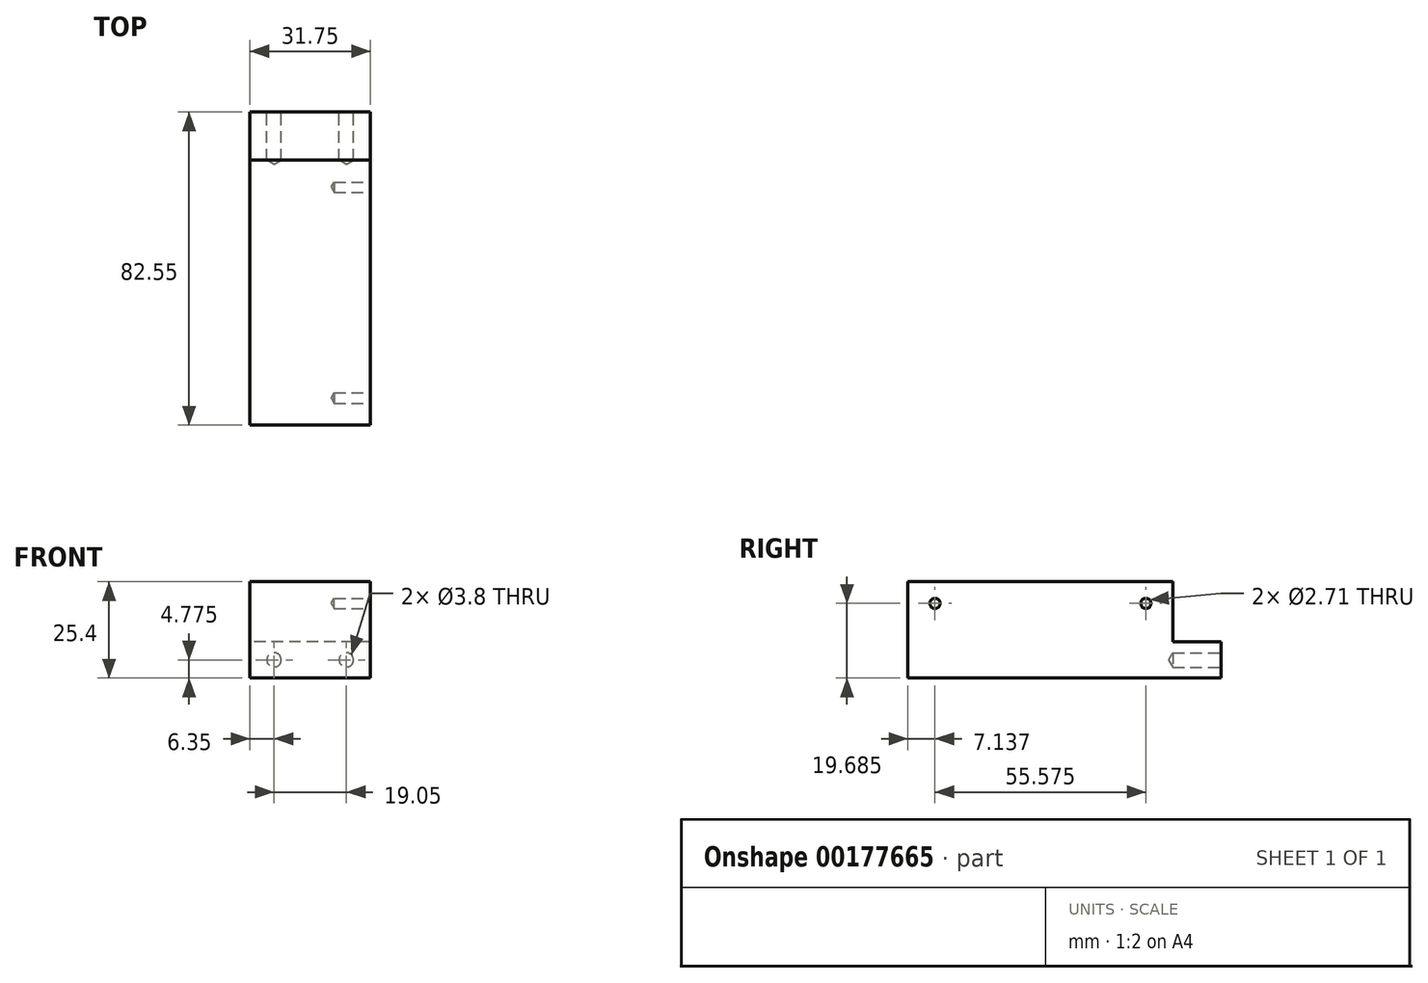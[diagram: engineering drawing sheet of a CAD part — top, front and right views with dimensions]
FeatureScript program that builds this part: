
annotation { "Feature Type Name" : "Feature", "Feature Type Description" : "" }
export const myFeature = defineFeature(function(context is Context, id is Id, definition is map)
    precondition{}
    {
        {
            var Q0;
            Q0=qCreatedBy(makeId("Top.planeOp"),FACE);
            var sketch = newSketch(context, id + "F0", { "sketchPlane" : qUnion([Q0])});
            skLineSegment(sketch, "E0.bottom", {"start": v(0, 0) * mm, "end": v(31.75, 0) * mm});
            skLineSegment(sketch, "E0.top", {"start": v(0, -82.55) * mm, "end": v(31.75, -82.55) * mm});
            skLineSegment(sketch, "E0.left", {"start": v(0, 0) * mm, "end": v(0, -82.55) * mm});
            skLineSegment(sketch, "E0.right", {"start": v(31.75, 0) * mm, "end": v(31.75, -82.55) * mm});
            skSolve(sketch);
        }
        {
            var Q0;
            Q0 = qSketchRegion(id + "F0", true);
            extrude(context, id + "F1", {"entities" : qUnion([Q0]), "depth" : 25.4 * mm});
        }
        {
            var Q0;
            Q0=makeQuery(id+"F1.opExtrude","SWEPT_FACE",FACE,{"disambiguationData":[OSD([sQuery(id+"F0.wireOp",EDGE,"E0.bottom")])]});
            var sketch = newSketch(context, id + "F2", { "sketchPlane" : qUnion([Q0])});
            skLineSegment(sketch, "E1.bottom", {"start": v(-31.75, 25.4) * mm, "end": v(0, 25.4) * mm});
            skLineSegment(sketch, "E1.top", {"start": v(-31.75, 9.53) * mm, "end": v(0, 9.53) * mm});
            skLineSegment(sketch, "E1.left", {"start": v(-31.75, 25.4) * mm, "end": v(-31.75, 9.53) * mm});
            skLineSegment(sketch, "E1.right", {"start": v(0, 25.4) * mm, "end": v(0, 9.53) * mm});
            skSolve(sketch);
        }
        {
            var Q0;
            Q0 = qSketchRegion(id + "F2", true);
            extrude(context, id + "F3", {"entities" : qUnion([Q0]), "operationType" : NewBodyOperationType.REMOVE, "oppositeDirection" : true, "depth" : 12.7 * mm});
        }
        {
            var Q0;
            Q0=makeQuery(id+"F1.opExtrude","SWEPT_FACE",FACE,{"disambiguationData":[OSD([sQuery(id+"F0.wireOp",EDGE,"E0.bottom")])]});
            var sketch = newSketch(context, id + "F4", { "sketchPlane" : qUnion([Q0])});
            skPoint(sketch, "E2", {"position": v(-25.4, 4.78) * mm});
            skPoint(sketch, "E3", {"position": v(-6.35, 4.78) * mm});
            skSolve(sketch);
        }
        {
            var Q0;
            Q0=sQuery(id+"F4.wireOp",VERTEX,"E2");
            var Q1;
            Q1=sQuery(id+"F4.wireOp",VERTEX,"E3");
            var Q2;
            Q2=makeQuery(id+"F1.opExtrude","SWEPT_BODY",BODY,{"disambiguationData":[OSD([sQuery(id+"F0.wireOp",EDGE,"E0.bottom"),sQuery(id+"F0.wireOp",EDGE,"E0.top"),sQuery(id+"F0.wireOp",EDGE,"E0.left"),sQuery(id+"F0.wireOp",EDGE,"E0.right")])]});
            hole(context, id + "F5", {"style" : HoleStyle.SIMPLE, "endStyle" : HoleEndStyle.BLIND, "standardTappedOrClearance" : lookupTablePath({ "standard" : "ANSI", "engagement" : "75%", "pitch" : "24 tpi", "size" : "#10", "type" : "Tapped" }), "standardBlindInLast" : lookupTablePath({ "standard" : "ANSI", "engagement" : "75%", "pitch" : "24 tpi", "size" : "#10", "type" : "Tapped" }), "holeDiameter" : 3.8 * mm, "holeDepth" : 12.7 * mm, "startFromSketch" : true, "locations" : qUnion([Q0, Q1]), "scope" : qUnion([Q2]), "majorDiameter" : 4.83 * mm});
        }
        {
            var Q0;
            Q0=makeQuery(id+"F1.opExtrude","SWEPT_FACE",FACE,{"disambiguationData":[OSD([sQuery(id+"F0.wireOp",EDGE,"E0.right")])]});
            var sketch = newSketch(context, id + "F6", { "sketchPlane" : qUnion([Q0])});
            skPoint(sketch, "E4", {"position": v(-19.84, 19.69) * mm});
            skPoint(sketch, "E5", {"position": v(-75.41, 19.69) * mm});
            skSolve(sketch);
        }
        {
            var Q0;
            Q0=sQuery(id+"F6.wireOp",VERTEX,"E4");
            var Q1;
            Q1=sQuery(id+"F6.wireOp",VERTEX,"E5");
            var Q2;
            Q2=makeQuery(id+"F1.opExtrude","SWEPT_BODY",BODY,{"disambiguationData":[OSD([sQuery(id+"F0.wireOp",EDGE,"E0.bottom"),sQuery(id+"F0.wireOp",EDGE,"E0.top"),sQuery(id+"F0.wireOp",EDGE,"E0.left"),sQuery(id+"F0.wireOp",EDGE,"E0.right")])]});
            hole(context, id + "F7", {"style" : HoleStyle.SIMPLE, "endStyle" : HoleEndStyle.BLIND, "standardTappedOrClearance" : lookupTablePath({ "standard" : "ANSI", "engagement" : "75%", "pitch" : "32 tpi", "size" : "#6", "type" : "Tapped" }), "standardBlindInLast" : lookupTablePath({ "standard" : "ANSI", "engagement" : "75%", "pitch" : "32 tpi", "size" : "#6", "type" : "Tapped" }), "holeDiameter" : 2.7 * mm, "holeDepth" : 9.52 * mm, "startFromSketch" : true, "locations" : qUnion([Q0, Q1]), "scope" : qUnion([Q2]), "majorDiameter" : 3.5 * mm});
        }
    });
